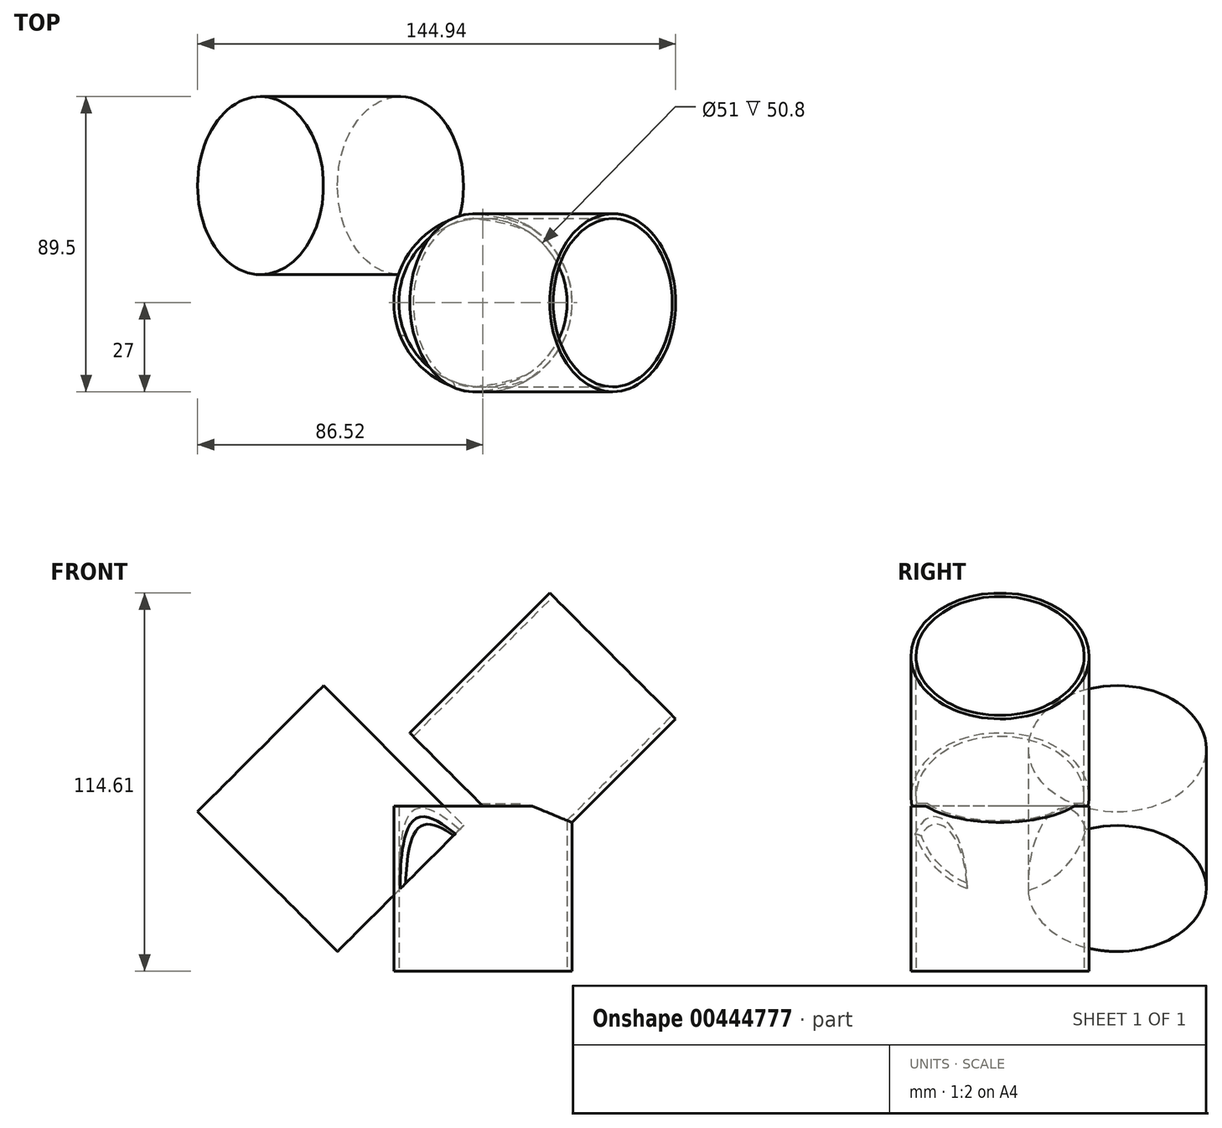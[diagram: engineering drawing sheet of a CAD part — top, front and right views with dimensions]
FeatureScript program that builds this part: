
annotation { "Feature Type Name" : "Feature", "Feature Type Description" : "" }
export const myFeature = defineFeature(function(context is Context, id is Id, definition is map)
    precondition{}
    {
        {
            var Q0;
            Q0=qCreatedBy(makeId("Top.planeOp"),FACE);
            var sketch = newSketch(context, id + "F0", { "sketchPlane" : qUnion([Q0])});
            skCircle(sketch, "E0", {"center": v(0, 0) * mm, "radius": 27 * mm});
            skSolve(sketch);
        }
        {
            var Q0;
            Q0 = qSketchRegion(id + "F0", true);
            extrude(context, id + "F1", {"entities" : qUnion([Q0]), "depth" : 50 * mm});
        }
        {
            var Q0;
            Q0=makeQuery(id+"F1.opExtrude","CAP_FACE",FACE,{"disambiguationData":[OSD([sQuery(id+"F0.wireOp",EDGE,"E0")])],"isStart":false});
            var sketch = newSketch(context, id + "F2", { "sketchPlane" : qUnion([Q0])});
            skLineSegment(sketch, "E1", {"start": v(0, 27) * mm, "end": v(0, -27) * mm});
            skSolve(sketch);
        }
        {
            var Q0;
            Q0=sQuery(id+"F2.wireOp",EDGE,"E1");
            cPlane(context, id + "F3", {"entities" : qUnion([Q0]), "cplaneType" : CPlaneType.LINE_ANGLE, "offset" : 25.4 * mm, "angle" : 45 * degree, "width" : 152.4 * mm, "height" : 152.4 * mm});
        }
        {
            var Q0;
            Q0=sQuery(id+"F2.wireOp",EDGE,"E1");
            cPlane(context, id + "F4", {"entities" : qUnion([Q0]), "cplaneType" : CPlaneType.LINE_ANGLE, "offset" : 25.4 * mm, "angle" : 135 * degree, "width" : 152.4 * mm, "height" : 152.4 * mm});
        }
        {
            var Q0;
            Q0=qCreatedBy(id+"F3.planeOp",FACE);
            var sketch = newSketch(context, id + "F5", { "sketchPlane" : qUnion([Q0])});
            skCircle(sketch, "E2", {"center": v(35.5, 0) * mm, "radius": 27 * mm});
            skSolve(sketch);
        }
        {
            var Q0;
            Q0=makeQuery(id+"F5.imprint","IMPRINT",FACE,{"disambiguationData":[TD([[makeQuery(id+"F5.imprint","IMPRINT",EDGE,{"derivedFrom":sQuery(id+"F5.wireOp",EDGE,"E2")}),1.0]])]});
            extrude(context, id + "F6", {"entities" : qUnion([Q0]), "operationType" : NewBodyOperationType.ADD, "oppositeDirection" : true, "depth" : 60 * mm});
        }
        {
            var Q0;
            Q0=qCreatedBy(id+"F4.planeOp",FACE);
            var sketch = newSketch(context, id + "F7", { "sketchPlane" : qUnion([Q0])});
            skCircle(sketch, "E3", {"center": v(0, 39.73) * mm, "radius": 27 * mm});
            skSolve(sketch);
        }
        {
            var Q0;
            Q0 = qSketchRegion(id + "F7", true);
            extrude(context, id + "F8", {"entities" : qUnion([Q0]), "operationType" : NewBodyOperationType.ADD, "depth" : 60 * mm});
        }
        {
            var Q0;
            Q0=makeQuery(id+"F6.opExtrude","CAP_FACE",FACE,{"disambiguationData":[OSD([sQuery(id+"F5.wireOp",EDGE,"E2")])],"isStart":false});
            var sketch = newSketch(context, id + "F9", { "sketchPlane" : qUnion([Q0])});
            skCircle(sketch, "E4", {"center": v(35.5, 0) * mm, "radius": 25.5 * mm});
            skSolve(sketch);
        }
        {
            var Q0;
            Q0 = qSketchRegion(id + "F9", true);
            extrude(context, id + "F10", {"entities" : qUnion([Q0]), "operationType" : NewBodyOperationType.REMOVE, "oppositeDirection" : true, "depth" : 60 * mm});
        }
        {
            var Q0;
            Q0=makeQuery(id+"F8.opExtrude","CAP_FACE",FACE,{"disambiguationData":[OSD([sQuery(id+"F7.wireOp",EDGE,"E3")])],"isStart":false});
            var sketch = newSketch(context, id + "F11", { "sketchPlane" : qUnion([Q0])});
            skCircle(sketch, "E5", {"center": v(0, 39.73) * mm, "radius": 25.5 * mm});
            skSolve(sketch);
        }
        {
            var Q0;
            Q0 = qSketchRegion(id + "F11", true);
            extrude(context, id + "F12", {"entities" : qUnion([Q0]), "operationType" : NewBodyOperationType.REMOVE, "oppositeDirection" : true, "depth" : 60 * mm});
        }
        {
            var Q0;
            Q0=makeQuery(id+"F1.opExtrude","CAP_FACE",FACE,{"disambiguationData":[OSD([sQuery(id+"F0.wireOp",EDGE,"E0")])],"isStart":true});
            var sketch = newSketch(context, id + "F13", { "sketchPlane" : qUnion([Q0])});
            skCircle(sketch, "E6", {"center": v(0, 0) * mm, "radius": 25.5 * mm});
            skSolve(sketch);
        }
        {
            var Q0;
            Q0 = qSketchRegion(id + "F13", true);
            extrude(context, id + "F14", {"entities" : qUnion([Q0]), "operationType" : NewBodyOperationType.REMOVE, "oppositeDirection" : true, "depth" : 50.8 * mm});
        }
    });
